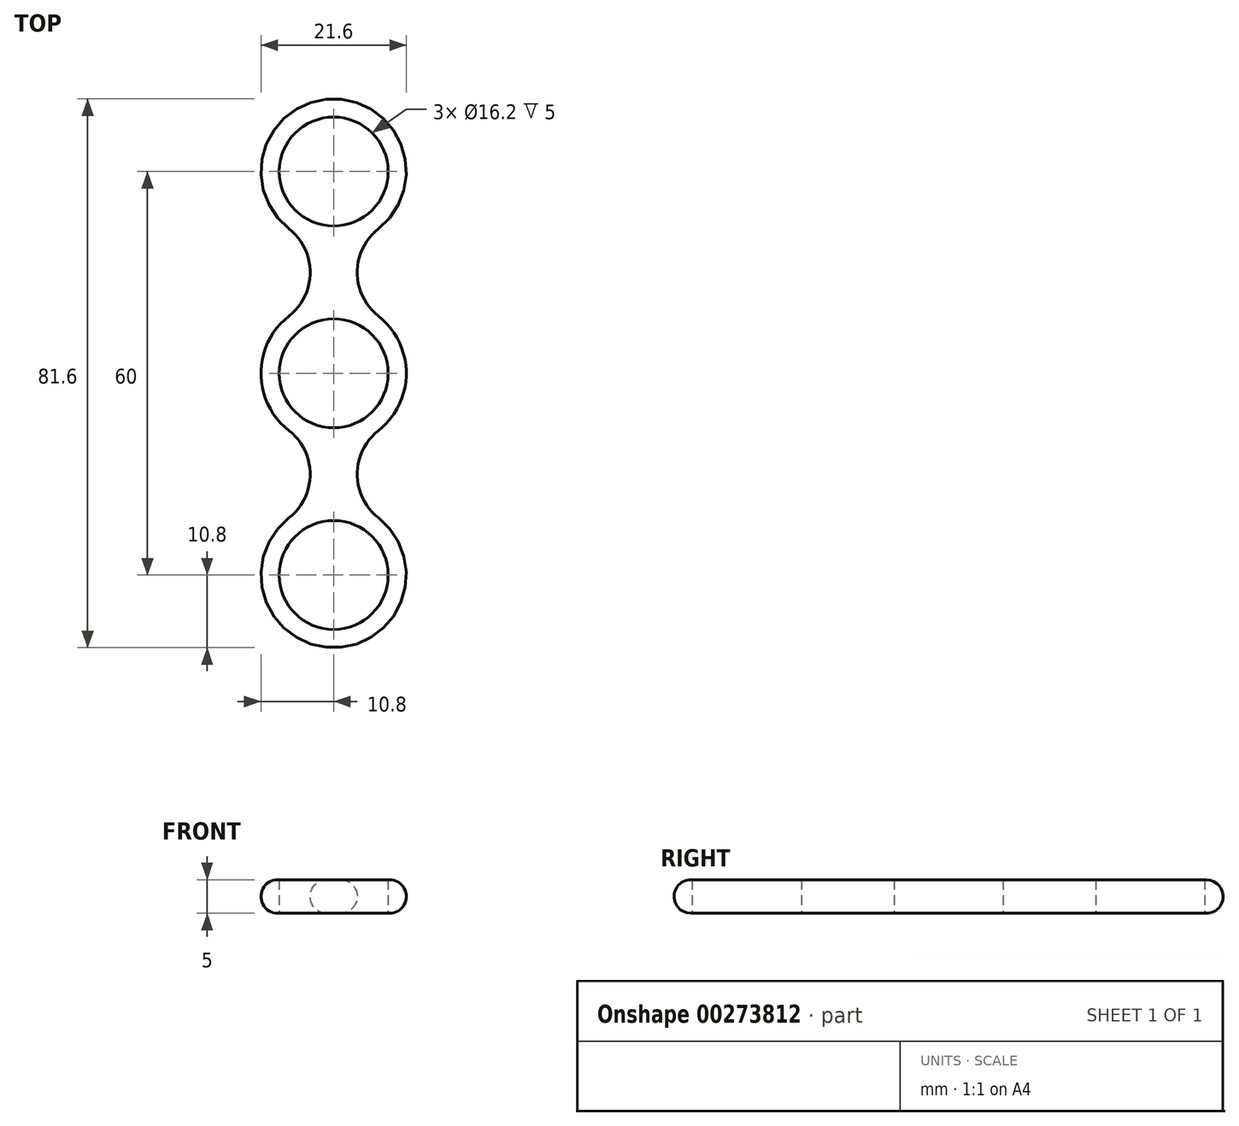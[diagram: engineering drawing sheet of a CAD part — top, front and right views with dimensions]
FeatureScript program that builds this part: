
annotation { "Feature Type Name" : "Feature", "Feature Type Description" : "" }
export const myFeature = defineFeature(function(context is Context, id is Id, definition is map)
    precondition{}
    {
        {
            var Q0;
            Q0=qCreatedBy(makeId("Top.planeOp"),FACE);
            var sketch = newSketch(context, id + "F0", { "sketchPlane" : qUnion([Q0])});
            skArc(sketch, "E0", {"start": v(-6.66, 8.5) * mm, "mid": v(-10.8, 0) * mm, "end": v(-6.66, -8.5) * mm});
            skLineSegment(sketch, "E1.anchor1", {"start": v(0, 0) * mm, "end": v(0, 30) * mm, "construction": true});
            skArc(sketch, "E2", {"start": v(6.66, 21.5) * mm, "mid": v(0, 40.8) * mm, "end": v(-6.66, 21.5) * mm});
            skLineSegment(sketch, "E3", {"start": v(-3.5, 15) * mm, "end": v(3.5, 15) * mm, "construction": true});
            skPoint(sketch, "E4", {"position": v(0, 15) * mm});
            skArc(sketch, "E5", {"start": v(-6.66, 8.5) * mm, "mid": v(-3.5, 15) * mm, "end": v(-6.66, 21.5) * mm});
            skPoint(sketch, "E5.second.point", {"position": v(-6.66, 21.5) * mm});
            skPoint(sketch, "E5.third.point", {"position": v(-6.66, 8.5) * mm});
            skArc(sketch, "E6.MirrorCS", {"start": v(6.66, 8.5) * mm, "mid": v(3.5, 15) * mm, "end": v(6.66, 21.5) * mm});
            skArc(sketch, "E7.1.0", {"start": v(-6.66, -21.5) * mm, "mid": v(0, -40.8) * mm, "end": v(6.66, -21.5) * mm});
            skArc(sketch, "E7.1.1", {"start": v(6.66, -8.5) * mm, "mid": v(3.5, -15) * mm, "end": v(6.66, -21.5) * mm});
            skArc(sketch, "E7.1.2", {"start": v(-6.66, -8.5) * mm, "mid": v(-3.5, -15) * mm, "end": v(-6.66, -21.5) * mm});
            skArc(sketch, "E8.trimOffspring", {"start": v(6.66, -8.5) * mm, "mid": v(10.8, 0) * mm, "end": v(6.66, 8.5) * mm});
            skArc(sketch, "E9.trimOffspring", {"start": v(6.66, -8.5) * mm, "mid": v(0, 10.8) * mm, "end": v(-6.66, -8.5) * mm});
            skSolve(sketch);
        }
        {
            var Q0;
            Q0 = qSketchRegion(id + "F0", true);
            extrude(context, id + "F1", {"entities" : qUnion([Q0]), "depth" : 5 * mm});
        }
        {
            var Q0;
            Q0=sQuery(id+"F0.wireOp",VERTEX,"E7.1.0.center");
            var Q1;
            Q1=sQuery(id+"F0.wireOp",VERTEX,"E7.2.0.center");
            var Q2;
            Q2=sQuery(id+"F0.wireOp",VERTEX,"E7.3.0.center");
            var Q3;
            Q3=sQuery(id+"F0.wireOp",VERTEX,"E0.center");
            var Q4;
            Q4=sQuery(id+"F0.wireOp",VERTEX,"E7.4.0.center");
            var Q5;
            Q5=sQuery(id+"F0.wireOp",VERTEX,"E1.anchor1.end");
            var Q6;
            Q6=sQuery(id+"F0.wireOp",VERTEX,"848ba9f9-12ce-4230-bfac-21e89cf6a5b4.5.2.0.center");
            var Q7;
            Q7=sQuery(id+"F0.wireOp",VERTEX,"eb815214-f97b-4861-be8c-82eb80d583a6.5.3.0.center");
            var Q8;
            Q8=sQuery(id+"F0.wireOp",VERTEX,"36e2516b-abf0-4b2d-9a40-534c7c5c5935.5.4.0.center");
            var Q9;
            Q9=sQuery(id+"F0.wireOp",VERTEX,"36e2516b-abf0-4b2d-9a40-534c7c5c5935.5.5.0.center");
            var Q10;
            Q10=sQuery(id+"F0.wireOp",VERTEX,"36e2516b-abf0-4b2d-9a40-534c7c5c5935.5.6.0.center");
            var Q11;
            Q11=sQuery(id+"F0.wireOp",VERTEX,"36e2516b-abf0-4b2d-9a40-534c7c5c5935.5.7.0.center");
            var Q12;
            Q12=makeQuery(id+"F1.opExtrude","SWEPT_BODY",BODY,{"disambiguationData":[OSD([sQuery(id+"F0.wireOp",EDGE,"E2"),sQuery(id+"F0.wireOp",EDGE,"E5"),sQuery(id+"F0.wireOp",EDGE,"E6.MirrorCS"),sQuery(id+"F0.wireOp",EDGE,"E7.1.0"),sQuery(id+"F0.wireOp",EDGE,"E7.1.1"),sQuery(id+"F0.wireOp",EDGE,"E7.1.2"),sQuery(id+"F0.wireOp",EDGE,"E7.2.0"),sQuery(id+"F0.wireOp",EDGE,"E7.2.1"),sQuery(id+"F0.wireOp",EDGE,"E7.2.2"),sQuery(id+"F0.wireOp",EDGE,"E7.3.0"),sQuery(id+"F0.wireOp",EDGE,"E7.3.1"),sQuery(id+"F0.wireOp",EDGE,"E7.3.2"),sQuery(id+"F0.wireOp",EDGE,"E7.4.0"),sQuery(id+"F0.wireOp",EDGE,"E7.4.1"),sQuery(id+"F0.wireOp",EDGE,"E7.4.2")])]});
            hole(context, id + "F2", {"style" : HoleStyle.SIMPLE, "endStyle" : HoleEndStyle.THROUGH, "oppositeDirection" : true, "holeDiameter" : 16.2 * mm, "tappedDepth" : 12 * mm, "tapClearance" : 3, "locations" : qUnion([Q0, Q1, Q2, Q3, Q4, Q5, Q6, Q7, Q8, Q9, Q10, Q11]), "scope" : qUnion([Q12])});
        }
        {
            var Q0;
            Q0=makeQuery(id+"F1.opExtrude","CAP_EDGE",EDGE,{"disambiguationData":[OSD([sQuery(id+"F0.wireOp",EDGE,"E7.1.0")])],"isStart":false});
            var Q1;
            Q1=makeQuery(id+"F1.opExtrude","CAP_EDGE",EDGE,{"disambiguationData":[OSD([sQuery(id+"F0.wireOp",EDGE,"E7.1.0")])],"isStart":true});
            var Q2;
            Q2=makeQuery(id+"F1.opExtrude","CAP_EDGE",EDGE,{"disambiguationData":[OSD([sQuery(id+"F0.wireOp",EDGE,"E5")])],"isStart":false});
            var Q3;
            Q3=makeQuery(id+"F1.opExtrude","CAP_EDGE",EDGE,{"disambiguationData":[OSD([sQuery(id+"F0.wireOp",EDGE,"E2")])],"isStart":false});
            var Q4;
            Q4=makeQuery(id+"F1.opExtrude","CAP_EDGE",EDGE,{"disambiguationData":[OSD([sQuery(id+"F0.wireOp",EDGE,"E7.4.1")])],"isStart":false});
            var Q5;
            Q5=makeQuery(id+"F1.opExtrude","CAP_EDGE",EDGE,{"disambiguationData":[OSD([sQuery(id+"F0.wireOp",EDGE,"E7.4.0")])],"isStart":false});
            var Q6;
            Q6=makeQuery(id+"F1.opExtrude","CAP_EDGE",EDGE,{"disambiguationData":[OSD([sQuery(id+"F0.wireOp",EDGE,"E7.3.1")])],"isStart":false});
            var Q7;
            Q7=makeQuery(id+"F1.opExtrude","CAP_EDGE",EDGE,{"disambiguationData":[OSD([sQuery(id+"F0.wireOp",EDGE,"E7.2.1")])],"isStart":false});
            var Q8;
            Q8=makeQuery(id+"F1.opExtrude","CAP_EDGE",EDGE,{"disambiguationData":[OSD([sQuery(id+"F0.wireOp",EDGE,"E7.2.2")])],"isStart":true});
            var Q9;
            Q9=makeQuery(id+"F1.opExtrude","CAP_EDGE",EDGE,{"disambiguationData":[OSD([sQuery(id+"F0.wireOp",EDGE,"E7.3.2")])],"isStart":true});
            var Q10;
            Q10=makeQuery(id+"F1.opExtrude","CAP_EDGE",EDGE,{"disambiguationData":[OSD([sQuery(id+"F0.wireOp",EDGE,"E7.4.2")])],"isStart":true});
            var Q11;
            Q11=makeQuery(id+"F1.opExtrude","CAP_EDGE",EDGE,{"disambiguationData":[OSD([sQuery(id+"F0.wireOp",EDGE,"E5")])],"isStart":true});
            fillet(context, id + "F3", {"entities" : qUnion([Q0, Q1, Q2, Q3, Q4, Q5, Q6, Q7, Q8, Q9, Q10, Q11]), "radius" : 2.5 * mm, "tangentPropagation" : true, "allowEdgeOverflow" : false});
        }
    });
